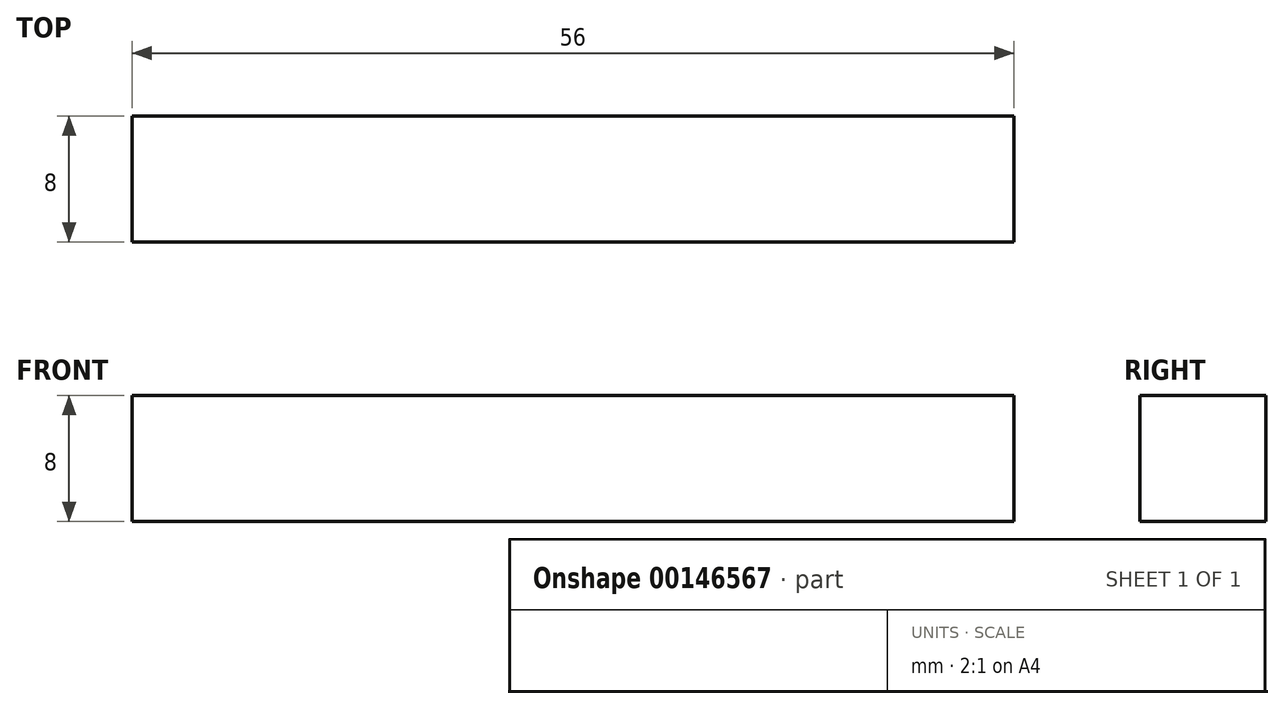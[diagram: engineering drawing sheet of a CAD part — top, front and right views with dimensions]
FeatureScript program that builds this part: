
annotation { "Feature Type Name" : "Feature", "Feature Type Description" : "" }
export const myFeature = defineFeature(function(context is Context, id is Id, definition is map)
    precondition{}
    {
        {
            assignVariable(context, id + "F0", {"name" : "width", "anyValue" : 8});
        }
        {
            var Q0;
            Q0=qCreatedBy(makeId("Front.planeOp"),FACE);
            var sketch = newSketch(context, id + "F1", { "sketchPlane" : qUnion([Q0])});
            skLineSegment(sketch, "E0", {"start": v(-28, 0) * mm, "end": v(-28, 8) * mm});
            skLineSegment(sketch, "E1", {"start": v(-28, 8) * mm, "end": v(28, 8) * mm});
            skLineSegment(sketch, "E2", {"start": v(28, 8) * mm, "end": v(28, 0) * mm});
            skLineSegment(sketch, "E3", {"start": v(28, 0) * mm, "end": v(-28, 0) * mm});
            skSolve(sketch);
        }
        {
            var Q0;
            Q0=makeQuery(id+"F1.imprint","IMPRINT",FACE,{"disambiguationData":[TD([[makeQuery(id+"F1.imprint","IMPRINT",EDGE,{"derivedFrom":sQuery(id+"F1.wireOp",EDGE,"E0")}),-1.0]])]});
            extrude(context, id + "F2", {"entities" : qUnion([Q0]), "depth" : (getVariable(context, 'width')) * mm, "symmetric" : true});
        }
    });
